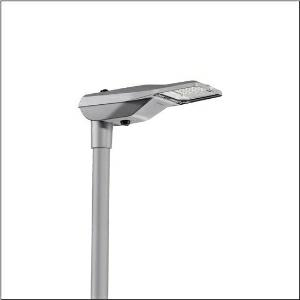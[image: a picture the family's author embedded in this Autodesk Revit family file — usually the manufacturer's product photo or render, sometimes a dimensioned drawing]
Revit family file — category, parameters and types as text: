
# Revit family: streetlight_sl_21_iq_micro___p0_8ab_5xe1r31y08cb_b23c
name_source: partatom
category: Lighting Fixtures
units: mm (PartAtom-declared; Revit-internal decimal feet)

## family parameters
Cut with Voids When Loaded = No
Host = Face
Light Source = No
Part Type = Normal
Room Calculation Point = No
Round Connector Dimension = Use Diameter
Shared = No

## types (1)
- --- (1 x LED, 2570 lm, 19.1 W, 3000K)
    Apparent Load = 19 VA
    CIE Flux Codes = 36 71 98 100 100
    Color Rendering = 70
    Color Temperature = 3000K
    Default Elevation = 1800 mm
    Description = Streetlight SL 21 iQ micro, mast luminaire, primary light control with lens, of PMMA, primary optical cover: cover, of toughened safety glass, transparent, light distribution: P0.8aB, light emission: direct distribution, primary light characteristic: asymmetric, installation type: post-top, side-entry, LED, High Power LED, rated luminous flux: 2.570lm, luminous efficacy: 135lm/W, light colour: 730, colour temperature: 3000K, control gear: iQ-Street Remote, D4i with power reduction, control: pre-setting: logarithmic dimming characteristic, Street-Remote, Auto-Match, Temp-Guard, Lumen-Switch, Night-Set, Smart-Wire, Light-Fading, Desk-Remote (wireless, voltage-free reading and setting of iQ features in the workshop via application-optimized NFC function/RFID function), optimised constant luminous flux control (CLO 2.0), mains connection: 220..240V, AC, 50/60Hz, start of lifetime: 19W, end of service life: 20W, reduction: 9W, luminaire housing, of diecast aluminium, powder-coated, SITECO metallic grey (DB 702S), corrosivity category C5 high according to DIN EN ISO 12944, please order mast flange separately, inclination adjustable: 0°, 5°, 10°, 15°, sealing non-destructively replaceable, multi-level sealing system, length: 528mm, width: 235mm, height: 110mm, mast flange for spigot size: 42mm (side-entry): 5XC10008XM4, 60/48mm (side-entry/post-top): 5XC10108XM2, 76/60mm (side-entry/post-top): 5XC10108XM1, mounting height: 4..8m, Smart Interface below and above, protection rating (complete): IP66, insulation class (complete): insulation class II (safety insulation), certification: CE, ENEC, ENEC+, VDE, impact resistance: IK10, permissible operating ambient temperature for outdoor applications: -40..+50°C, standard-compliant lighting for roads and squares, packaging unit: 1 piece

Light Distribution: P0.8aB
    Height = 110 mm
    Lamp = 1 x LED
    Lamp Light Flux = 2570 lm
    Lamp Power = 19.1 W
    Lamp count = 1
    Length = 528 mm
    Luminous efficacy = 135 lm/W
    Manufacturer = Siteco
    ModVariant = No
    Model = 5XE1R31Y08CB
    Number of Poles = 1
    OnlyDefault = Yes
    Power Factor = 1
    Product Name = Streetlight SL 21 iQ micro | P0.8aB
    Product group = mast luminaire | pylon top
    ProductGroupID = 6100
    Protection Class = Protection class II
    Protection Degree = IP 66
    RLX_Detail_Level = 1
    RLX_Emergency_Light_Flux = 0 lm
    RLX_Emergency_Type = 0
    RLX_Emergency_Type_DB = No
    RlxData = <blob elided: 98737 chars, md5=84169e2f>
    Socket = socket
    Standby Power = 0 W
    System Light Flux = 2570 lm
    System Power = 19 W
    Type Comments = factory setting: luminous flux: 100 % | dim-lin: 254 | 387 mA
    Type Image = l_1007239.jpg
    URL = http://relux.com
    VarID = @adj_083323
    Voltage = 0 V
    Weight = 0.00 kg
    Width = 235 mm

## geometry (parser evidence)
native form markers: Blend x4, Sweep x8
no freeform markers — native parametric forms only
